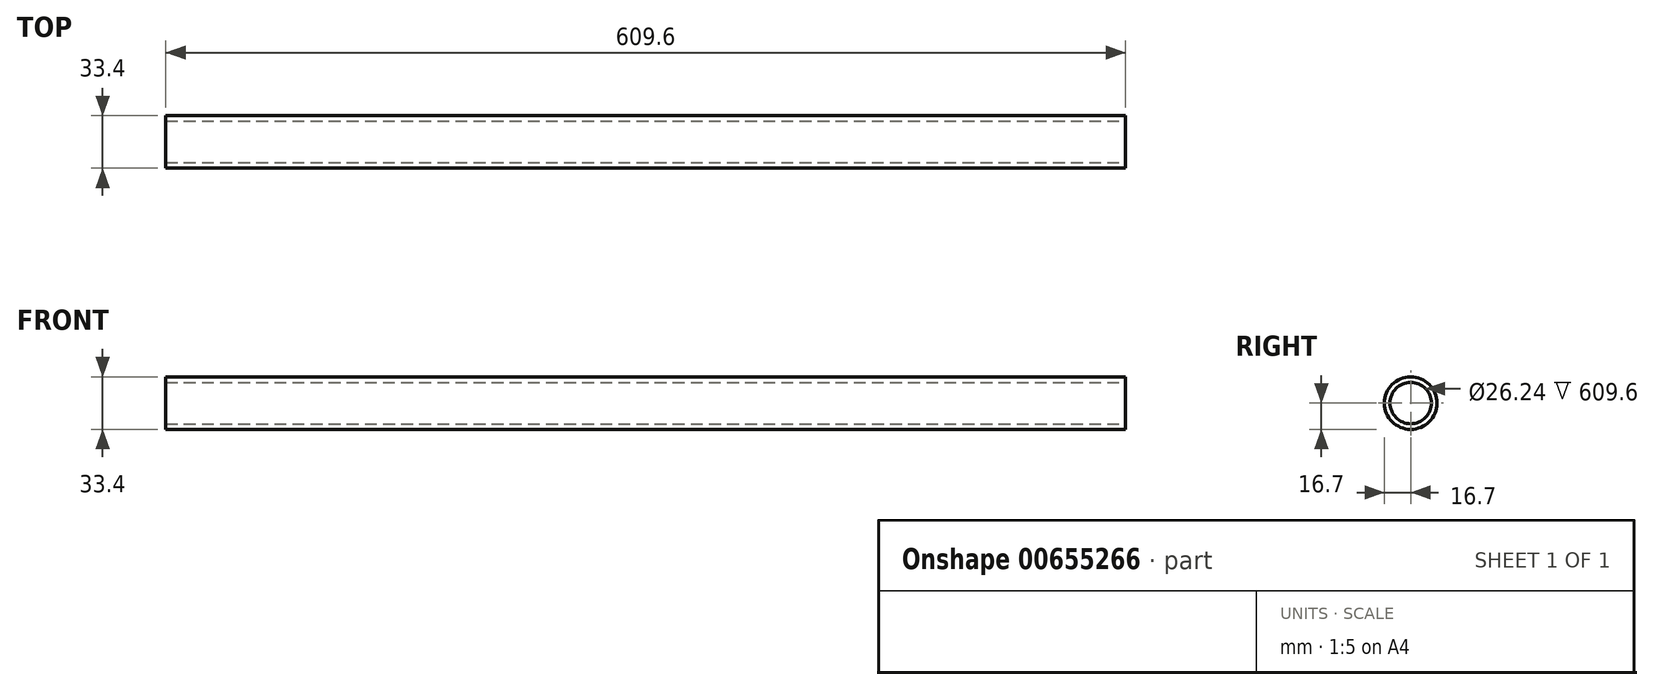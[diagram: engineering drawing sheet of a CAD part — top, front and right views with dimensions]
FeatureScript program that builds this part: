
annotation { "Feature Type Name" : "Feature", "Feature Type Description" : "" }
export const myFeature = defineFeature(function(context is Context, id is Id, definition is map)
    precondition{}
    {
        {
            var Q0;
            Q0=qCreatedBy(makeId("Right.planeOp"),FACE);
            var sketch = newSketch(context, id + "F0", { "sketchPlane" : qUnion([Q0])});
            skCircle(sketch, "E0", {"center": v(0, 0) * mm, "radius": 16.7 * mm});
            skCircle(sketch, "E1", {"center": v(0, 0) * mm, "radius": 13.12 * mm});
            skSolve(sketch);
        }
        {
            var Q0;
            Q0 = qSketchRegion(id + "F0", true);
            extrude(context, id + "F1", {"entities" : qUnion([Q0]), "oppositeDirection" : true, "depth" : 609.6 * mm, "offsetDistance" : 25.4 * mm});
        }
    });
